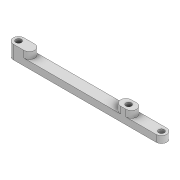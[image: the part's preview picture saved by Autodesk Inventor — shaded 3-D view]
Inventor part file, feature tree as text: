
AUTODESK INVENTOR PART (.ipt)
format: ipt  version: 2022 (Build 260153000, 153)  size: 123,392 bytes
history: native  units: mm
features: extrude x2, sketch x1, projected_geometry x1
ambient origin geometry x8: Origin, YZ Plane, XZ Plane, XY Plane, X Axis, Y Axis, Z Axis, Center Point
bodies: Solid1 (feature_tree)
feature tree (4):
  extrude  "Extrusion1"  Depth=8.0mm
  extrude  "Extrusion7"  Depth=5.0mm
  sketch  "Sketch2"  dims[d0=105.445mm d1=8.0mm d2=4.2mm d4=5.0mm d5=0.0mm d8=4.2mm d9=81.271mm d10=4.2mm d11=8.0mm d12=8.0mm d13=8.0mm d28=8.0mm d29=8.0mm d30=8.0mm d31=2.0mm d32=2.0mm d33=5.0mm d34=0.0mm]
  projected_geometry  "Projected Loop1"
